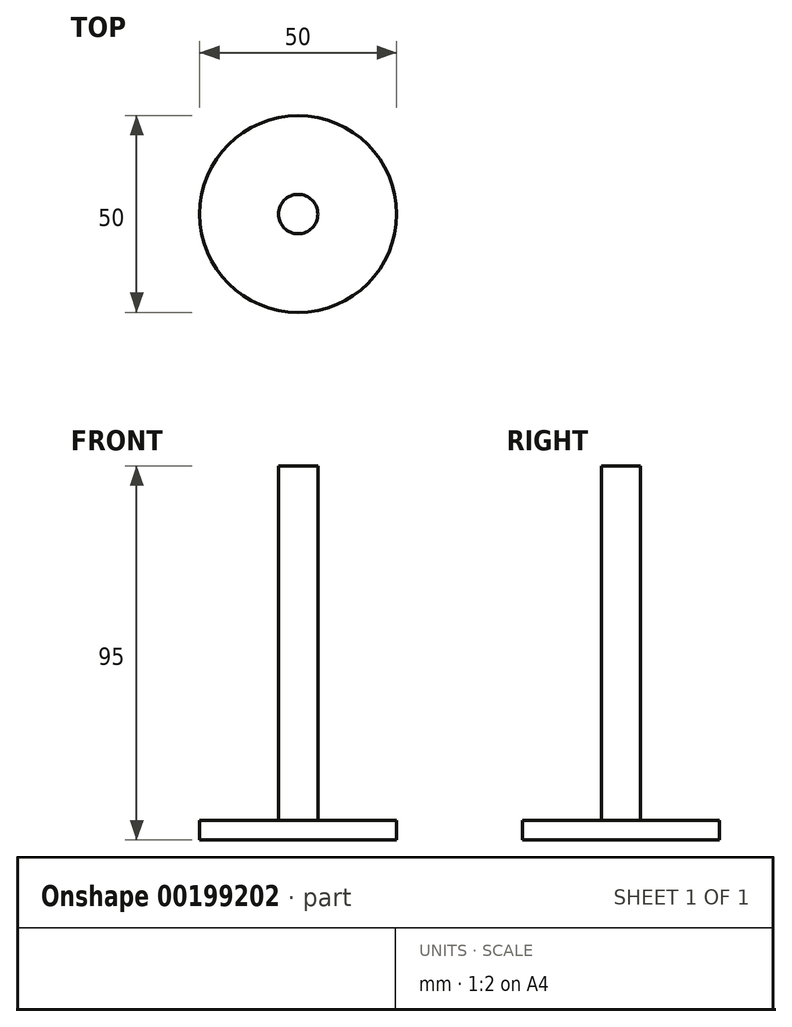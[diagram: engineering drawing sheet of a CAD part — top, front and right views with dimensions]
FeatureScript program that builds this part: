
annotation { "Feature Type Name" : "Feature", "Feature Type Description" : "" }
export const myFeature = defineFeature(function(context is Context, id is Id, definition is map)
    precondition{}
    {
        {
            var Q0;
            Q0=qCreatedBy(makeId("Top.planeOp"),FACE);
            var sketch = newSketch(context, id + "F0", { "sketchPlane" : qUnion([Q0])});
            skCircle(sketch, "E0", {"center": v(0, 0) * mm, "radius": 25 * mm});
            skSolve(sketch);
        }
        {
            var Q0;
            Q0 = qSketchRegion(id + "F0", true);
            extrude(context, id + "F1", {"entities" : qUnion([Q0]), "depth" : 5 * mm});
        }
        {
            var Q0;
            Q0=makeQuery(id+"F1.opExtrude","CAP_FACE",FACE,{"disambiguationData":[OSD([sQuery(id+"F0.wireOp",EDGE,"E0")])],"isStart":false});
            var sketch = newSketch(context, id + "F2", { "sketchPlane" : qUnion([Q0])});
            skCircle(sketch, "E1", {"center": v(0, 0) * mm, "radius": 5 * mm});
            skSolve(sketch);
        }
        {
            var Q0;
            Q0 = qSketchRegion(id + "F2", true);
            extrude(context, id + "F3", {"entities" : qUnion([Q0]), "operationType" : NewBodyOperationType.ADD, "depth" : 90 * mm});
        }
        {
            var Q0;
            Q0=makeQuery(id+"F3.opExtrude","CAP_FACE",FACE,{"disambiguationData":[OSD([sQuery(id+"F2.wireOp",EDGE,"E1")])],"isStart":false});
            var sketch = newSketch(context, id + "F4", { "sketchPlane" : qUnion([Q0])});
            skLineSegment(sketch, "E2", {"start": v(-5, 0) * mm, "end": v(5, 0) * mm});
            skSolve(sketch);
        }
        {
            var Q0;
            Q0 = qSketchRegion(id + "F4", true);
            var Q1;
            Q1=sQuery(id+"F4.wireOp",EDGE,"E2");
            extrude(context, id + "F5", {"entities" : qUnion([Q0]), "bodyType" : ExtendedToolBodyType.SURFACE, "surfaceEntities" : qUnion([Q1]), "depth" : 15 * mm});
        }
    });
